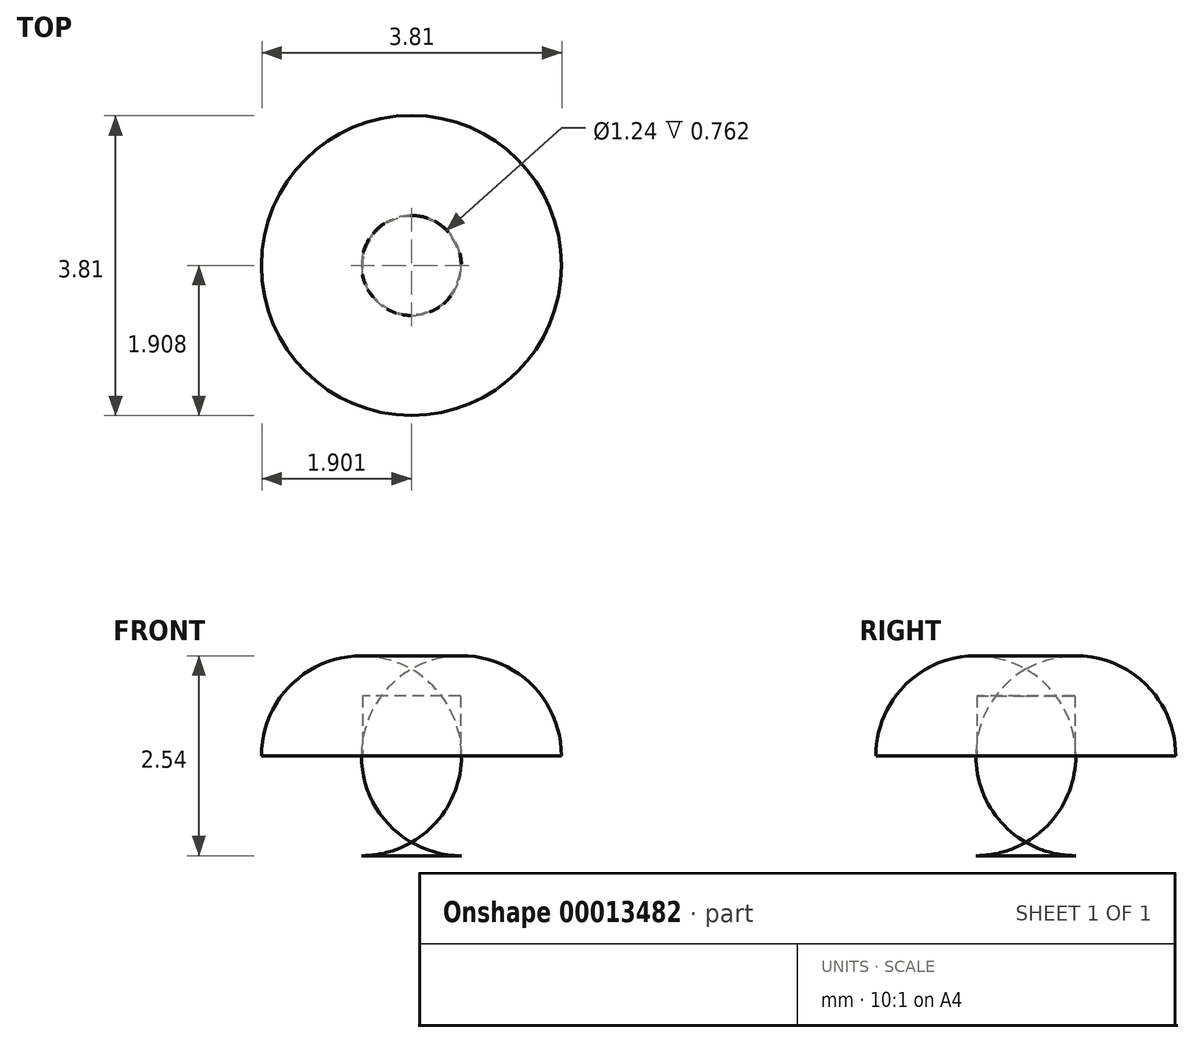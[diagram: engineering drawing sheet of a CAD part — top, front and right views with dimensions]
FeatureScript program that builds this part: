
annotation { "Feature Type Name" : "Feature", "Feature Type Description" : "" }
export const myFeature = defineFeature(function(context is Context, id is Id, definition is map)
    precondition{}
    {
        {
            var Q0;
            Q0=qCreatedBy(makeId("Top.planeOp"),FACE);
            var sketch = newSketch(context, id + "F0", { "sketchPlane" : qUnion([Q0])});
            skCircle(sketch, "E0", {"center": v(-116.57, -43.32) * mm, "radius": 1.9 * mm});
            skSolve(sketch);
        }
        {
            var Q0;
            Q0=makeQuery(id+"F0.imprint","IMPRINT",FACE,{"disambiguationData":[TD([[makeQuery(id+"F0.imprint","IMPRINT",EDGE,{"derivedFrom":sQuery(id+"F0.wireOp",EDGE,"E0")}),1.0]])]});
            extrude(context, id + "F1", {"entities" : qUnion([Q0]), "depth" : 1.27 * mm});
        }
        {
            var Q0;
            Q0=makeQuery(id+"F1.opExtrude","CAP_FACE",FACE,{"disambiguationData":[OSD([sQuery(id+"F0.wireOp",EDGE,"E0")])],"isStart":false});
            var sketch = newSketch(context, id + "F2", { "sketchPlane" : qUnion([Q0])});
            skCircle(sketch, "E1", {"center": v(-116.57, -43.32) * mm, "radius": 0.62 * mm});
            skSolve(sketch);
        }
        {
            var Q0;
            Q0=makeQuery(id+"F2.imprint","IMPRINT",FACE,{"disambiguationData":[TD([[makeQuery(id+"F2.imprint","IMPRINT",EDGE,{"derivedFrom":sQuery(id+"F2.wireOp",EDGE,"E1")}),1.0]])]});
            extrude(context, id + "F3", {"entities" : qUnion([Q0]), "operationType" : NewBodyOperationType.ADD, "depth" : 0.76 * mm});
        }
        {
            var Q0;
            Q0=makeQuery(id+"F1.opExtrude","CAP_EDGE",EDGE,{"disambiguationData":[OSD([sQuery(id+"F0.wireOp",EDGE,"E0")])],"isStart":true});
            fillet(context, id + "F4", {"entities" : qUnion([Q0]), "radius" : 1.27 * mm, "tangentPropagation" : true, "allowEdgeOverflow" : false});
        }
    });
